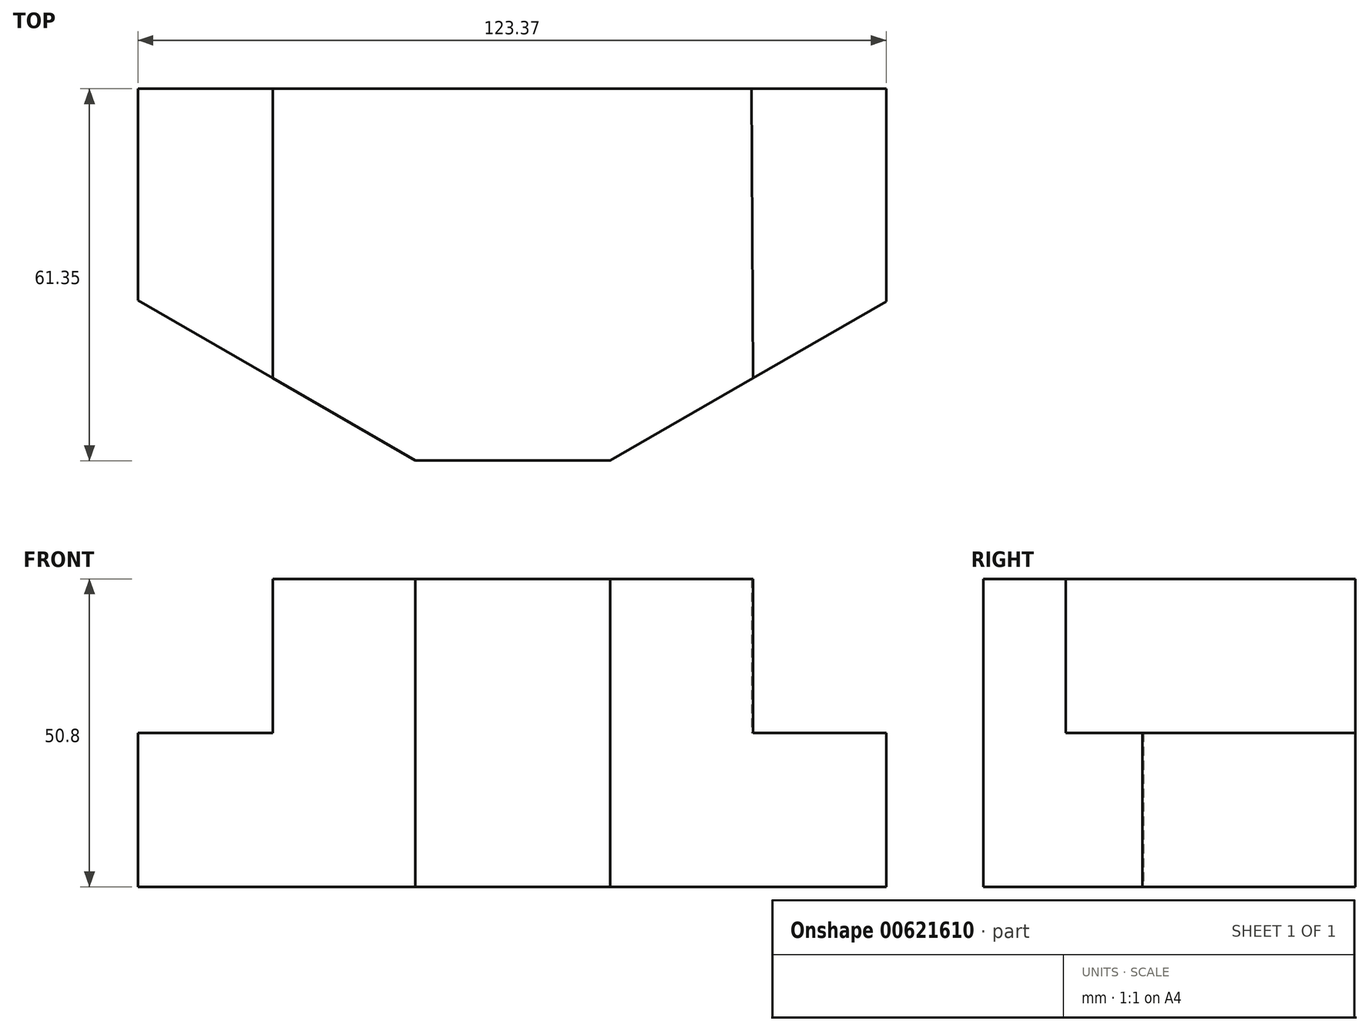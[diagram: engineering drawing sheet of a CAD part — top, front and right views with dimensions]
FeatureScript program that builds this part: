
annotation { "Feature Type Name" : "Feature", "Feature Type Description" : "" }
export const myFeature = defineFeature(function(context is Context, id is Id, definition is map)
    precondition{}
    {
        {
            var Q0;
            Q0=qCreatedBy(makeId("Top.planeOp"),FACE);
            var sketch = newSketch(context, id + "F0", { "sketchPlane" : qUnion([Q0])});
            skLineSegment(sketch, "E0", {"start": v(0, 0) * mm, "end": v(0, -34.93) * mm});
            skLineSegment(sketch, "E1", {"start": v(45.76, -61.35) * mm, "end": v(77.86, -61.35) * mm});
            skLineSegment(sketch, "E2", {"start": v(123.37, -35.07) * mm, "end": v(123.37, 0) * mm});
            skLineSegment(sketch, "E3", {"start": v(123.37, 0) * mm, "end": v(0, 0) * mm});
            skPoint(sketch, "E4.end.orphan", {"position": v(123.37, -30.67) * mm});
            skLineSegment(sketch, "E5", {"start": v(123.37, 0) * mm, "end": v(123.37, -35.07) * mm});
            skLineSegment(sketch, "E6", {"start": v(123.37, 0) * mm, "end": v(100.44, 0) * mm});
            skLineSegment(sketch, "E7", {"start": v(0, 0) * mm, "end": v(22.88, 0) * mm});
            skLineSegment(sketch, "E8", {"start": v(100.44, 0) * mm, "end": v(76.2, 0) * mm});
            skLineSegment(sketch, "E9", {"start": v(22.88, 0) * mm, "end": v(45.76, 0) * mm});
            skLineSegment(sketch, "E10", {"start": v(0, -34.93) * mm, "end": v(45.76, -61.35) * mm});
            skLineSegment(sketch, "E11", {"start": v(77.86, -61.35) * mm, "end": v(123.37, -35.07) * mm});
            skPoint(sketch, "E12.orphan", {"position": v(123.37, -61.35) * mm});
            skSolve(sketch);
        }
        {
            var Q0;
            Q0 = qSketchRegion(id + "F0", true);
            extrude(context, id + "F1", {"entities" : qUnion([Q0]), "depth" : 25.4 * mm, "offsetDistance" : 25.4 * mm});
        }
        {
            var Q0;
            Q0=makeQuery(id+"F1.opExtrude","CAP_FACE",FACE,{"disambiguationData":[OSD([sQuery(id+"F0.wireOp",EDGE,"E3"),sQuery(id+"F0.wireOp",EDGE,"E5"),sQuery(id+"F0.wireOp",EDGE,"E0"),sQuery(id+"F0.wireOp",EDGE,"E6"),sQuery(id+"F0.wireOp",EDGE,"E7"),sQuery(id+"F0.wireOp",EDGE,"E8"),sQuery(id+"F0.wireOp",EDGE,"E9"),sQuery(id+"F0.wireOp",EDGE,"E1"),sQuery(id+"F0.wireOp",EDGE,"E10"),sQuery(id+"F0.wireOp",EDGE,"E11")])],"isStart":false});
            var sketch = newSketch(context, id + "F2", { "sketchPlane" : qUnion([Q0])});
            skLineSegment(sketch, "E13", {"start": v(0, 0) * mm, "end": v(22.23, 0) * mm});
            skLineSegment(sketch, "E14", {"start": v(101.14, 0) * mm, "end": v(123.37, 0) * mm});
            skLineSegment(sketch, "E15", {"start": v(22.23, 0) * mm, "end": v(22.23, -47.76) * mm});
            skLineSegment(sketch, "E16", {"start": v(101.4, -47.76) * mm, "end": v(101.14, 0) * mm});
            skSolve(sketch);
        }
        {
            var Q0;
            Q0 = qSketchRegion(id + "F2", true);
            var Q1;
            {var subQ0=sQuery(id+"F2.wireOp",EDGE,"E15");Q1=makeQuery(id+"F2.imprint","IMPRINT",FACE,{"disambiguationData":[TD([[makeQuery(id+"F2.imprint","IMPRINT",EDGE,{"derivedFrom":subQ0}),1.0]])]});}
            extrude(context, id + "F3", {"entities" : qUnion([Q0, Q1]), "operationType" : NewBodyOperationType.ADD, "depth" : 25.4 * mm, "offsetDistance" : 25.4 * mm});
        }
    });
